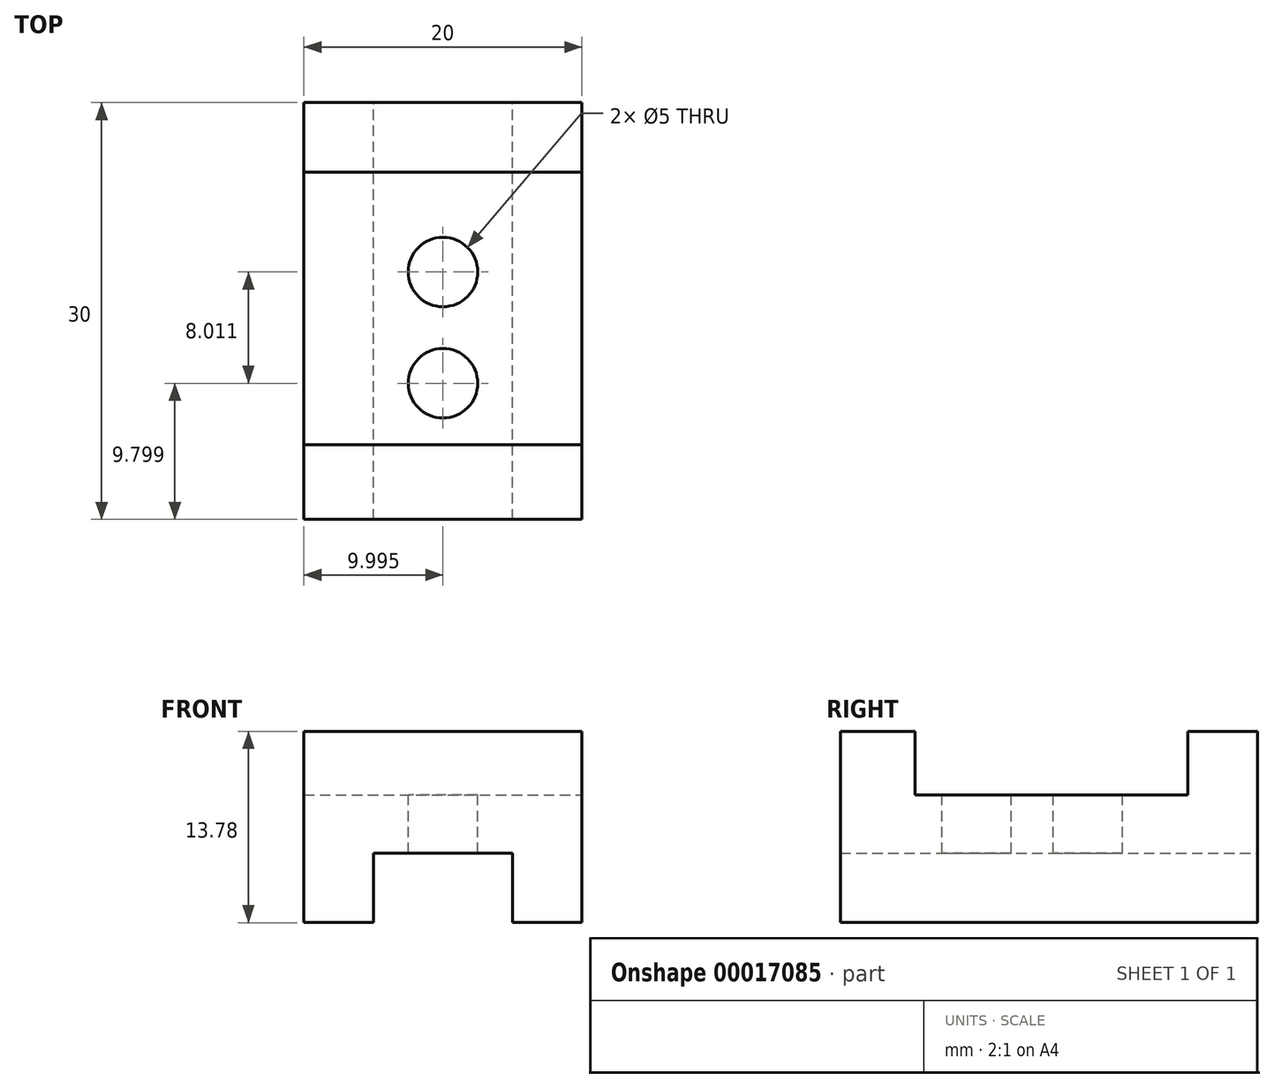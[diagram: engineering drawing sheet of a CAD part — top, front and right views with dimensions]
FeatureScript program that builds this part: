
annotation { "Feature Type Name" : "Feature", "Feature Type Description" : "" }
export const myFeature = defineFeature(function(context is Context, id is Id, definition is map)
    precondition{}
    {
        {
            var Q0;
            Q0=qCreatedBy(makeId("Front.planeOp"),FACE);
            var sketch = newSketch(context, id + "F0", { "sketchPlane" : qUnion([Q0])});
            skLineSegment(sketch, "E0", {"start": v(-35.11, -10.67) * mm, "end": v(-30.11, -10.67) * mm});
            skLineSegment(sketch, "E1", {"start": v(-30.11, -10.67) * mm, "end": v(-30.11, -5.67) * mm});
            skLineSegment(sketch, "E2", {"start": v(-30.11, -5.67) * mm, "end": v(-20.11, -5.67) * mm});
            skLineSegment(sketch, "E3", {"start": v(-20.11, -5.67) * mm, "end": v(-20.11, -10.67) * mm});
            skLineSegment(sketch, "E4", {"start": v(-20.11, -10.67) * mm, "end": v(-15.11, -10.67) * mm});
            skLineSegment(sketch, "E5", {"start": v(-15.11, -10.67) * mm, "end": v(-15.11, 3.1) * mm});
            skLineSegment(sketch, "E6", {"start": v(-15.11, 3.1) * mm, "end": v(-35.11, 3.1) * mm});
            skLineSegment(sketch, "E7", {"start": v(-35.11, 3.1) * mm, "end": v(-35.11, -10.67) * mm});
            skSolve(sketch);
        }
        {
            var Q0;
            Q0=makeQuery(id+"F0.imprint","IMPRINT",FACE,{"disambiguationData":[TD([[makeQuery(id+"F0.imprint","IMPRINT",EDGE,{"derivedFrom":sQuery(id+"F0.wireOp",EDGE,"E0")}),1.0]])]});
            extrude(context, id + "F1", {"entities" : qUnion([Q0]), "depth" : 30 * mm});
        }
        {
            var Q0;
            Q0=makeQuery(id+"F1.opExtrude","SWEPT_FACE",FACE,{"disambiguationData":[OSD([sQuery(id+"F0.wireOp",EDGE,"E5")])]});
            var sketch = newSketch(context, id + "F2", { "sketchPlane" : qUnion([Q0])});
            skLineSegment(sketch, "E8", {"start": v(-24.63, 3.1) * mm, "end": v(-24.63, -1.49) * mm});
            skLineSegment(sketch, "E9", {"start": v(-24.63, -1.49) * mm, "end": v(-5, -1.49) * mm});
            skLineSegment(sketch, "E10", {"start": v(-5, -1.49) * mm, "end": v(-5, 3.1) * mm});
            skLineSegment(sketch, "E11", {"start": v(-24.63, 3.1) * mm, "end": v(-5, 3.1) * mm});
            skSolve(sketch);
        }
        {
            var Q0;
            Q0 = qSketchRegion(id + "F2", true);
            extrude(context, id + "F3", {"entities" : qUnion([Q0]), "operationType" : NewBodyOperationType.REMOVE, "endBound" : BoundingType.THROUGH_ALL, "oppositeDirection" : true, "depth" : 25 * mm});
        }
        {
            var Q0;
            Q0=makeQuery(id+"F3.boolean.opBoolean","COPY",FACE,{"derivedFrom":makeQuery(id+"F3.opExtrude","SWEPT_FACE",FACE,{"disambiguationData":[OSD([sQuery(id+"F2.wireOp",EDGE,"E9")])]})});
            var sketch = newSketch(context, id + "F4", { "sketchPlane" : qUnion([Q0])});
            skCircle(sketch, "E12", {"center": v(-25.11, -12.19) * mm, "radius": 2.5 * mm});
            skCircle(sketch, "E13", {"center": v(-25.11, -20.2) * mm, "radius": 2.5 * mm});
            skSolve(sketch);
        }
        {
            var Q0;
            Q0 = qSketchRegion(id + "F4", true);
            extrude(context, id + "F5", {"entities" : qUnion([Q0]), "operationType" : NewBodyOperationType.REMOVE, "endBound" : BoundingType.THROUGH_ALL, "oppositeDirection" : true, "depth" : 25 * mm});
        }
    });
